# Revit family: CM0196821CocinaKalavi150Der
name_source: partatom
category: Specialty Equipment
units: mm (PartAtom-declared; Revit-internal decimal feet)

## family parameters
Always vertical = Yes
Cut with Voids When Loaded = No
Part Type = Normal
Room Calculation Point = No
Round Connector Dimension = Use Diameter
Shared = No
Work Plane-Based = No

## types (1)
- CM0196821CocinaKalavi150Der
    Carga Máxima Mueble Inferior = 47 kg
    Carga Máxima Mueble Superior = 26 kg
    Creado por = IDD
    Description = Cocina lista para armar, muy práctica, cómoda y funcional.
Se destaca su diseño contemporáneo en color Duna, un color de madera claro y con vetas marcadas,
dando un aspecto muy natural y acorde a las últimas tendencias en decoración, sus manijas y patas
negrasque contrastan, le dan un toque industrial que complementa el diseño de la Cocina.
Sus nichos brindan espacios decorativos y de almacenamiento tan útiles en las cocinas abiertas
que invitan a tenerlas integradas con el área social.
    Fecha de Creacion = 09/10/2020
    Garantía = 1 año en madera y herrajes
    Manufacturer = Corona
    Material Accesorios = Corona_Acero_Negro Mate
    Material Aglomerado = Corona_Madera_Coñac
    Material Interior = Corona_Madera_Blanco
    Peso Neto Aprox Módulo Inf = 47 kg
    Peso Neto Aprox Módulo Sup = 26 kg
    Referencia = CM0196821
    Resistencia = Mueble resistente al rayado y la abrasión
    Resistencia a la Humedad = hinchamiento < o =8%
    URL = https://corona.co

## geometry (parser evidence)
native form markers: Sweep x14
no freeform markers — native parametric forms only
